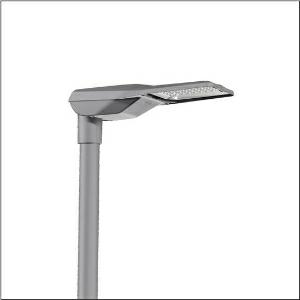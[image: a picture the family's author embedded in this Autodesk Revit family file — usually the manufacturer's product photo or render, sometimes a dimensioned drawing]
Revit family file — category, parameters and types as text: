
# Revit family: streetlight_sl_21_iq_mini___st0_8a_5xe2c31d08jb_69b6
name_source: partatom
category: Lighting Fixtures
units: mm (PartAtom-declared; Revit-internal decimal feet)

## family parameters
Cut with Voids When Loaded = No
Host = Face
Light Source = No
Part Type = Normal
Room Calculation Point = No
Round Connector Dimension = Use Diameter
Shared = No

## types (1)
- --- (1 x LED, 10820 lm, 71.6 W, 3000K)
    Apparent Load = 72 VA
    CIE Flux Codes = 41 75 97 100 100
    Color Rendering = 70
    Color Temperature = 3000K
    Default Elevation = 1800 mm
    Description = Streetlight SL 21 iQ mini, mast luminaire, primary light control with lens, of PMMA, primary optical cover: cover, of toughened safety glass, transparent, light distribution: ST0.8a, light emission: direct distribution, primary light characteristic: asymmetric, installation type: post-top, side-entry, LED, High Power LED, rated luminous flux: 10.820lm, luminous efficacy: 151lm/W, light colour: 730, colour temperature: 3000K, control gear: iQ-Comfort, control: Auto-Match, Temp-Guard, Lumen-Switch, Night-Set, Smart-Wire, Light-Fading, Desk-Remote (wireless, voltage-free reading and setting of iQ features in the workshop via application-optimized NFC function/RFID function), optimised constant luminous flux control (CLO 2.0), pre-setting: linear dimming characteristic, mains connection: 220..240V, AC, 50/60Hz, start of lifetime: 72W, end of service life: 75W, reduction: 33W, luminaire housing, of diecast aluminium, powder-coated, SITECO metallic grey (DB 702S), corrosivity category C5 high according to DIN EN ISO 12944, please order mast flange separately, inclination adjustable: 0°, 5°, 10°, 15°, sealing non-destructively replaceable, multi-level sealing system, length: 628mm, width: 235mm, height: 110mm, mast flange for spigot size: 42mm (side-entry): 5XC10008XM4, 60/48mm (side-entry/post-top): 5XC10108XM2, 76/60mm (side-entry/post-top): 5XC10108XM1, mounting height: 4..8m, protection rating (complete): IP66, insulation class (complete): insulation class II (safety insulation), certification: CE, ENEC, ENEC+, VDE, impact resistance: IK10, permissible operating ambient temperature for outdoor applications: -40..+50°C, standard-compliant lighting for roads and squares, packaging unit: 1 piece

Light Distribution: ST0.8a
    Height = 110 mm
    Lamp = 1 x LED
    Lamp Light Flux = 10820 lm
    Lamp Power = 71.6 W
    Lamp count = 1
    Length = 625 mm
    Luminous efficacy = 151 lm/W
    Manufacturer = Siteco
    ModVariant = No
    Model = 5XE2C31D08JB
    Number of Poles = 1
    OnlyDefault = Yes
    Power Factor = 1
    Product Name = Streetlight SL 21 iQ mini | ST0.8a
    Product group = mast luminaire | pylon top
    ProductGroupID = 6100
    Protection Class = Protection class II
    Protection Degree = IP 66
    RLX_Detail_Level = 1
    RLX_Emergency_Light_Flux = 0 lm
    RLX_Emergency_Type = 0
    RLX_Emergency_Type_DB = No
    RlxData = <blob elided: 26361 chars, md5=9609d1d5>
    Socket = socket
    Standby Power = 0 W
    System Light Flux = 10820 lm
    System Power = 72 W
    Type Comments = factory setting: luminous flux: 100 % | dim-lin: 254 | 746 mA
    Type Image = l_1003519.jpg
    URL = http://relux.com
    VarID = @adj_168783
    Voltage = 0 V
    Weight = 0.00 kg
    Width = 234 mm

## geometry (parser evidence)
native form markers: Blend x4, Sweep x9
no freeform markers — native parametric forms only
